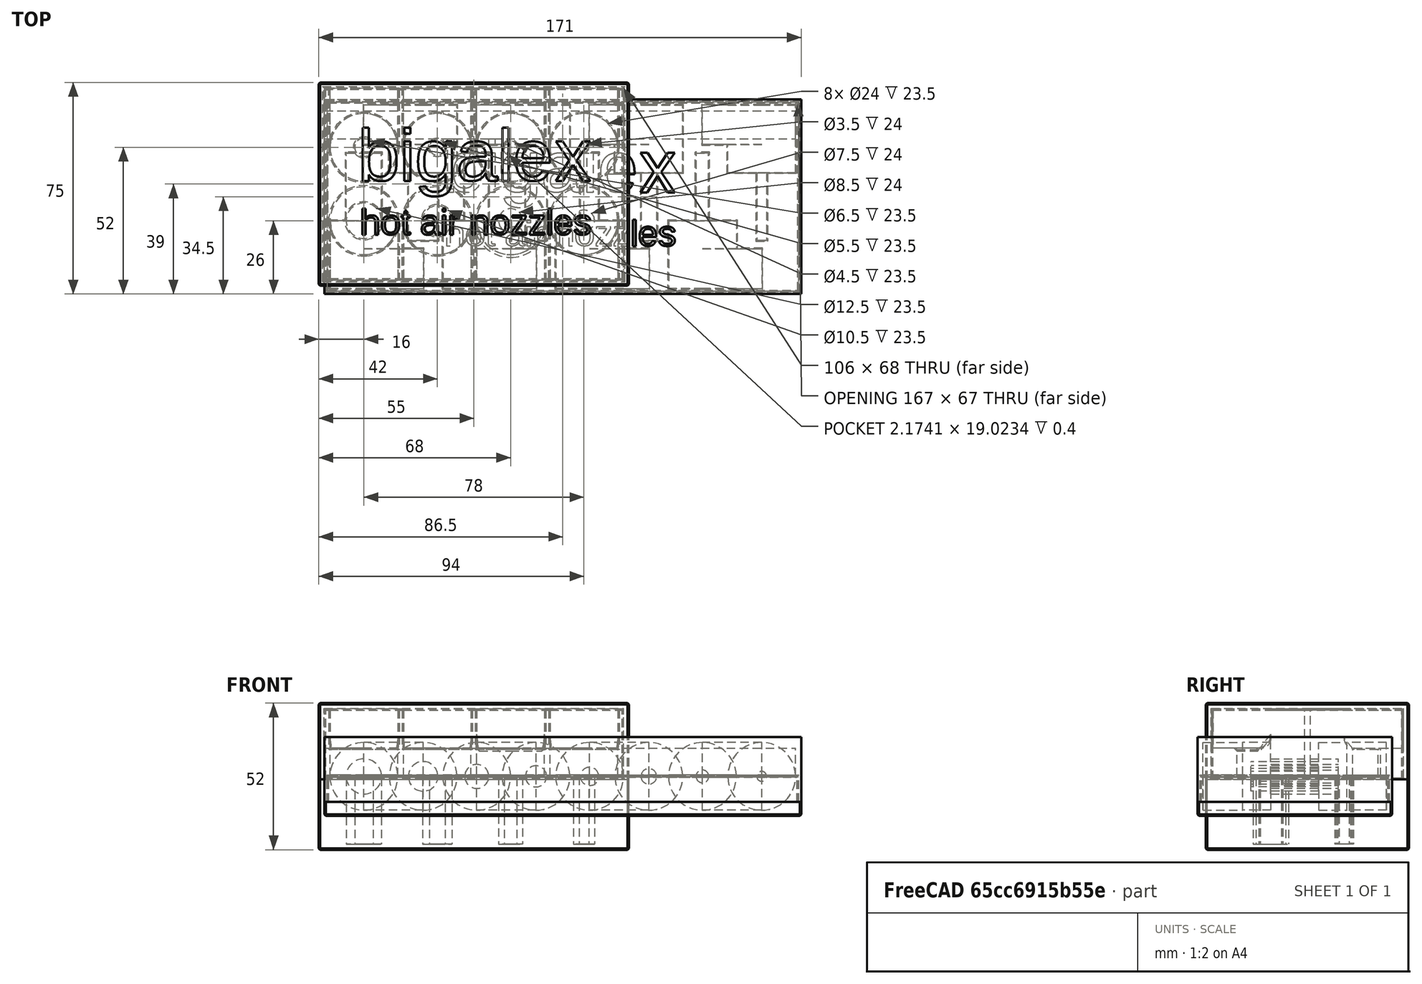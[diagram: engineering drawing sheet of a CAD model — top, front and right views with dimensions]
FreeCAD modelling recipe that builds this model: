
FCSTD DOCUMENT  (FreeCAD 0.18R16093 (Git))
Label: hotair
License: All rights reserved
LicenseURL: http://en.wikipedia.org/wiki/All_rights_reserved
objects: Part::Cylinder×32, Part::Box×27, Part::MultiFuse×26, Part::Cut×8, Part::Part2DObjectPython×6, Part::Extrusion×6, Part::Chamfer×5, Part::FeaturePython×3, PartDesign::Body×1
note: 114 computed .brp shape members not serialized (recipe doc carries the construction recipe); baked Part::Feature solids carry a one-line shape summary decoded from their .brp

FEATURE [PartDesign::Body] Body
  Origin = -> Origin
FEATURE [Part::Cylinder] Cylinder  label="smallcyl"
  Angle = 360
  AttacherType = Attacher::AttachEngine3D
  Height = 24
  Placement = pos=(0,0,0) rot=(1,0,0;1.5708rad)
  Radius = 12
FEATURE [Part::Cylinder] Cylinder001  label="bigcyl"
  Angle = 360
  AttacherType = Attacher::AttachEngine3D
  Height = 24
  Placement = pos=(0,0,0) rot=(-1,0,0;1.5708rad)
  Radius = 5.25
FEATURE [Part::Box] Box  label="Cube"
  AttacherType = Attacher::AttachEngine3D
  Height = 24
  Length = 21
  Placement = pos=(0,-24,-12) rot=(0,0,1;0rad)
  Width = 14
FEATURE [Part::MultiFuse] Fusion
  Placement = pos=(21,17,0) rot=(0,0,1;3.14159rad)
  Shapes = -> [Cylinder,Cylinder001,Box]
FEATURE [Part::Box] Box001  label="Cube001"
  AttacherType = Attacher::AttachEngine3D
  Height = 24
  Length = 21
  Placement = pos=(0,-24,-12) rot=(0,0,1;0rad)
  Width = 14
FEATURE [Part::Cylinder] Cylinder002  label="smallcyl001"
  Angle = 360
  AttacherType = Attacher::AttachEngine3D
  Height = 24
  Placement = pos=(0,0,0) rot=(1,0,0;1.5708rad)
  Radius = 12
FEATURE [Part::Cylinder] Cylinder003  label="bigcyl001"
  Angle = 360
  AttacherType = Attacher::AttachEngine3D
  Height = 24
  Placement = pos=(0,0,0) rot=(-1,0,0;1.5708rad)
  Radius = 6.25
FEATURE [Part::MultiFuse] Fusion001
  Shapes = -> [Cylinder002,Cylinder003,Box001]
FEATURE [Part::MultiFuse] Fusion002
  Shapes = -> [Fusion,Fusion001]
FEATURE [Part::Cylinder] Cylinder004  label="smallcyl002"
  Angle = 360
  AttacherType = Attacher::AttachEngine3D
  Height = 24
  Placement = pos=(0,0,0) rot=(1,0,0;1.5708rad)
  Radius = 12
FEATURE [Part::Box] Box002  label="Cube002"
  AttacherType = Attacher::AttachEngine3D
  Height = 24
  Length = 21
  Placement = pos=(0,-24,-12) rot=(0,0,1;0rad)
  Width = 14
FEATURE [Part::Box] Box003  label="Cube003"
  AttacherType = Attacher::AttachEngine3D
  Height = 24
  Length = 21
  Placement = pos=(0,-24,-12) rot=(0,0,1;0rad)
  Width = 14
FEATURE [Part::Cylinder] Cylinder005  label="smallcyl003"
  Angle = 360
  AttacherType = Attacher::AttachEngine3D
  Height = 24
  Placement = pos=(0,0,0) rot=(1,0,0;1.5708rad)
  Radius = 12
FEATURE [Part::Cylinder] Cylinder006  label="bigcyl002"
  Angle = 360
  AttacherType = Attacher::AttachEngine3D
  Height = 24
  Placement = pos=(0,0,0) rot=(-1,0,0;1.5708rad)
  Radius = 3.75
FEATURE [Part::MultiFuse] Fusion003
  Placement = pos=(21,17,0) rot=(0,0,1;3.14159rad)
  Shapes = -> [Cylinder005,Cylinder006,Box003]
FEATURE [Part::Cylinder] Cylinder007  label="bigcyl003"
  Angle = 360
  AttacherType = Attacher::AttachEngine3D
  Height = 24
  Placement = pos=(0,0,0) rot=(-1,0,0;1.5708rad)
  Radius = 4.25
FEATURE [Part::MultiFuse] Fusion004
  Shapes = -> [Cylinder004,Cylinder007,Box002]
FEATURE [Part::MultiFuse] Fusion005
  Placement = pos=(40,0,0) rot=(0,0,1;0rad)
  Shapes = -> [Fusion003,Fusion004]
FEATURE [Part::Cylinder] Cylinder008  label="smallcyl004"
  Angle = 360
  AttacherType = Attacher::AttachEngine3D
  Height = 24
  Placement = pos=(0,0,0) rot=(1,0,0;1.5708rad)
  Radius = 12
FEATURE [Part::Box] Box004  label="Cube004"
  AttacherType = Attacher::AttachEngine3D
  Height = 24
  Length = 21
  Placement = pos=(0,-24,-12) rot=(0,0,1;0rad)
  Width = 14
FEATURE [Part::Box] Box005  label="Cube005"
  AttacherType = Attacher::AttachEngine3D
  Height = 24
  Length = 21
  Placement = pos=(0,-24,-12) rot=(0,0,1;0rad)
  Width = 14
FEATURE [Part::Cylinder] Cylinder009  label="smallcyl005"
  Angle = 360
  AttacherType = Attacher::AttachEngine3D
  Height = 24
  Placement = pos=(0,0,0) rot=(1,0,0;1.5708rad)
  Radius = 12
FEATURE [Part::Cylinder] Cylinder010  label="bigcyl004"
  Angle = 360
  AttacherType = Attacher::AttachEngine3D
  Height = 24
  Placement = pos=(0,0,0) rot=(-1,0,0;1.5708rad)
  Radius = 2.75
FEATURE [Part::MultiFuse] Fusion006
  Placement = pos=(21,17,0) rot=(0,0,1;3.14159rad)
  Shapes = -> [Cylinder009,Cylinder010,Box005]
FEATURE [Part::Cylinder] Cylinder011  label="bigcyl005"
  Angle = 360
  AttacherType = Attacher::AttachEngine3D
  Height = 24
  Placement = pos=(0,0,0) rot=(-1,0,0;1.5708rad)
  Radius = 3.25
FEATURE [Part::MultiFuse] Fusion007
  Shapes = -> [Cylinder008,Cylinder011,Box004]
FEATURE [Part::MultiFuse] Fusion008
  Placement = pos=(80,0,0) rot=(0,0,1;0rad)
  Shapes = -> [Fusion006,Fusion007]
FEATURE [Part::Cylinder] Cylinder012  label="smallcyl006"
  Angle = 360
  AttacherType = Attacher::AttachEngine3D
  Height = 24
  Placement = pos=(0,0,0) rot=(1,0,0;1.5708rad)
  Radius = 12
FEATURE [Part::Box] Box006  label="Cube006"
  AttacherType = Attacher::AttachEngine3D
  Height = 24
  Length = 21
  Placement = pos=(0,-24,-12) rot=(0,0,1;0rad)
  Width = 14
FEATURE [Part::Box] Box007  label="Cube007"
  AttacherType = Attacher::AttachEngine3D
  Height = 24
  Length = 21
  Placement = pos=(0,-24,-12) rot=(0,0,1;0rad)
  Width = 14
FEATURE [Part::Cylinder] Cylinder013  label="smallcyl007"
  Angle = 360
  AttacherType = Attacher::AttachEngine3D
  Height = 24
  Placement = pos=(0,0,0) rot=(1,0,0;1.5708rad)
  Radius = 12
FEATURE [Part::Cylinder] Cylinder014  label="bigcyl006"
  Angle = 360
  AttacherType = Attacher::AttachEngine3D
  Height = 24
  Placement = pos=(0,0,0) rot=(-1,0,0;1.5708rad)
  Radius = 1.75
FEATURE [Part::MultiFuse] Fusion009
  Placement = pos=(21,17,0) rot=(0,0,1;3.14159rad)
  Shapes = -> [Cylinder013,Cylinder014,Box007]
FEATURE [Part::Cylinder] Cylinder015  label="bigcyl007"
  Angle = 360
  AttacherType = Attacher::AttachEngine3D
  Height = 24
  Placement = pos=(0,0,0) rot=(-1,0,0;1.5708rad)
  Radius = 2.25
FEATURE [Part::MultiFuse] Fusion010
  Shapes = -> [Cylinder012,Cylinder015,Box006]
FEATURE [Part::MultiFuse] Fusion011
  Placement = pos=(120,0,0) rot=(0,0,1;0rad)
  Shapes = -> [Fusion009,Fusion010]
FEATURE [Part::Box] Box008  label="Cube008"
  AttacherType = Attacher::AttachEngine3D
  Height = 10
  Length = 167
  Placement = pos=(-14,29,0) rot=(0,0,1;0rad)
  Width = 10
FEATURE [Part::Cylinder] Cylinder016  label="smallcyl008"
  Angle = 360
  AttacherType = Attacher::AttachEngine3D
  Height = 24
  Placement = pos=(0,0,0) rot=(1,0,0;1.5708rad)
  Radius = 12
FEATURE [Part::Box] Box009  label="Cube009"
  AttacherType = Attacher::AttachEngine3D
  Height = 24
  Length = 21
  Placement = pos=(0,-24,-12) rot=(0,0,1;0rad)
  Width = 14
FEATURE [Part::Cylinder] Cylinder017  label="bigcyl008"
  Angle = 360
  AttacherType = Attacher::AttachEngine3D
  Height = 24
  Placement = pos=(0,0,0) rot=(-1,0,0;1.5708rad)
  Radius = 6.25
FEATURE [Part::MultiFuse] Fusion013  label="nozzle000"
  Placement = pos=(0,0,0) rot=(0.57735,-0.57735,0.57735;4.18879rad)
  Shapes = -> [Cylinder016,Cylinder017,Box009]
FEATURE [Part::Cylinder] Cylinder018  label="bigcyl009"
  Angle = 360
  AttacherType = Attacher::AttachEngine3D
  Height = 24
  Placement = pos=(0,0,0) rot=(-1,0,0;1.5708rad)
  Radius = 3.25
FEATURE [Part::Box] Box010  label="Cube010"
  AttacherType = Attacher::AttachEngine3D
  Height = 24
  Length = 21
  Placement = pos=(0,-24,-12) rot=(0,0,1;0rad)
  Width = 14
FEATURE [Part::Cylinder] Cylinder019  label="smallcyl009"
  Angle = 360
  AttacherType = Attacher::AttachEngine3D
  Height = 24
  Placement = pos=(0,0,0) rot=(1,0,0;1.5708rad)
  Radius = 12
FEATURE [Part::MultiFuse] Fusion014  label="nozzle001"
  Placement = pos=(0,26,0) rot=(0.57735,0.57735,-0.57735;4.18879rad)
  Shapes = -> [Cylinder019,Cylinder018,Box010]
FEATURE [Part::Cylinder] Cylinder020  label="bigcyl010"
  Angle = 360
  AttacherType = Attacher::AttachEngine3D
  Height = 24
  Placement = pos=(0,0,0) rot=(-1,0,0;1.5708rad)
  Radius = 5.25
FEATURE [Part::Box] Box011  label="Cube011"
  AttacherType = Attacher::AttachEngine3D
  Height = 24
  Length = 21
  Placement = pos=(0,-24,-12) rot=(0,0,1;0rad)
  Width = 14
FEATURE [Part::Cylinder] Cylinder021  label="smallcyl010"
  Angle = 360
  AttacherType = Attacher::AttachEngine3D
  Height = 24
  Placement = pos=(0,0,0) rot=(1,0,0;1.5708rad)
  Radius = 12
FEATURE [Part::Cylinder] Cylinder022  label="bigcyl011"
  Angle = 360
  AttacherType = Attacher::AttachEngine3D
  Height = 24
  Placement = pos=(0,0,0) rot=(-1,0,0;1.5708rad)
  Radius = 2.75
FEATURE [Part::Cylinder] Cylinder023  label="smallcyl011"
  Angle = 360
  AttacherType = Attacher::AttachEngine3D
  Height = 24
  Placement = pos=(0,0,0) rot=(1,0,0;1.5708rad)
  Radius = 12
FEATURE [Part::MultiFuse] Fusion015  label="nozzle002"
  Placement = pos=(26,0,0) rot=(0.57735,-0.57735,0.57735;4.18879rad)
  Shapes = -> [Cylinder023,Cylinder020,Box011]
FEATURE [Part::Box] Box012  label="Cube012"
  AttacherType = Attacher::AttachEngine3D
  Height = 24
  Length = 21
  Placement = pos=(0,-24,-12) rot=(0,0,1;0rad)
  Width = 14
FEATURE [Part::MultiFuse] Fusion016  label="nozzle003"
  Placement = pos=(26,26,0) rot=(0.57735,0.57735,-0.57735;4.18879rad)
  Shapes = -> [Cylinder021,Cylinder022,Box012]
FEATURE [Part::Cylinder] Cylinder024  label="bigcyl012"
  Angle = 360
  AttacherType = Attacher::AttachEngine3D
  Height = 24
  Placement = pos=(0,0,0) rot=(-1,0,0;1.5708rad)
  Radius = 4.25
FEATURE [Part::Box] Box013  label="Cube013"
  AttacherType = Attacher::AttachEngine3D
  Height = 24
  Length = 21
  Placement = pos=(0,-24,-12) rot=(0,0,1;0rad)
  Width = 14
FEATURE [Part::Cylinder] Cylinder025  label="smallcyl012"
  Angle = 360
  AttacherType = Attacher::AttachEngine3D
  Height = 24
  Placement = pos=(0,0,0) rot=(1,0,0;1.5708rad)
  Radius = 12
FEATURE [Part::Cylinder] Cylinder026  label="bigcyl013"
  Angle = 360
  AttacherType = Attacher::AttachEngine3D
  Height = 24
  Placement = pos=(0,0,0) rot=(-1,0,0;1.5708rad)
  Radius = 2.25
FEATURE [Part::Cylinder] Cylinder027  label="smallcyl013"
  Angle = 360
  AttacherType = Attacher::AttachEngine3D
  Height = 24
  Placement = pos=(0,0,0) rot=(1,0,0;1.5708rad)
  Radius = 12
FEATURE [Part::MultiFuse] Fusion017  label="nozzle004"
  Placement = pos=(52,0,0) rot=(0.57735,-0.57735,0.57735;4.18879rad)
  Shapes = -> [Cylinder027,Cylinder024,Box013]
FEATURE [Part::Box] Box014  label="Cube014"
  AttacherType = Attacher::AttachEngine3D
  Height = 24
  Length = 21
  Placement = pos=(0,-24,-12) rot=(0,0,1;0rad)
  Width = 14
FEATURE [Part::MultiFuse] Fusion018  label="nozzle005"
  Placement = pos=(52,26,0) rot=(0.57735,0.57735,-0.57735;4.18879rad)
  Shapes = -> [Cylinder025,Cylinder026,Box014]
FEATURE [Part::Cylinder] Cylinder028  label="bigcyl014"
  Angle = 360
  AttacherType = Attacher::AttachEngine3D
  Height = 24
  Placement = pos=(0,0,0) rot=(-1,0,0;1.5708rad)
  Radius = 3.75
FEATURE [Part::Box] Box015  label="Cube015"
  AttacherType = Attacher::AttachEngine3D
  Height = 24
  Length = 21
  Placement = pos=(0,-24,-12) rot=(0,0,1;0rad)
  Width = 14
FEATURE [Part::Cylinder] Cylinder029  label="smallcyl014"
  Angle = 360
  AttacherType = Attacher::AttachEngine3D
  Height = 24
  Placement = pos=(0,0,0) rot=(1,0,0;1.5708rad)
  Radius = 12
FEATURE [Part::Cylinder] Cylinder030  label="bigcyl015"
  Angle = 360
  AttacherType = Attacher::AttachEngine3D
  Height = 24
  Placement = pos=(0,0,0) rot=(-1,0,0;1.5708rad)
  Radius = 1.75
FEATURE [Part::Cylinder] Cylinder031  label="smallcyl015"
  Angle = 360
  AttacherType = Attacher::AttachEngine3D
  Height = 24
  Placement = pos=(0,0,0) rot=(1,0,0;1.5708rad)
  Radius = 12
FEATURE [Part::MultiFuse] Fusion019  label="nozzle006"
  Placement = pos=(78,0,0) rot=(0.57735,-0.57735,0.57735;4.18879rad)
  Shapes = -> [Cylinder031,Cylinder028,Box015]
FEATURE [Part::Box] Box016  label="Cube016"
  AttacherType = Attacher::AttachEngine3D
  Height = 24
  Length = 21
  Placement = pos=(0,-24,-12) rot=(0,0,1;0rad)
  Width = 14
FEATURE [Part::MultiFuse] Fusion020  label="nozzle007"
  Placement = pos=(78,26,0) rot=(0.57735,0.57735,-0.57735;4.18879rad)
  Shapes = -> [Cylinder029,Cylinder030,Box016]
FEATURE [Part::MultiFuse] Fusion021  label="nozzles2"
  Shapes = -> [Fusion013,Fusion014,Fusion015,Fusion016,Fusion017,Fusion018,Fusion019,Fusion020]
FEATURE [Part::Box] Box017  label="Cube017"
  AttacherType = Attacher::AttachEngine3D
  Height = 50
  Length = 106
  Placement = pos=(-14,-21,-26) rot=(0,0,1;0rad)
  Width = 68
FEATURE [Part::Box] Box018  label="lidkeepout"
  AttacherType = Attacher::AttachEngine3D
  Height = 25.1
  Length = 106.2
  Placement = pos=(-14.1,-21.1,-1) rot=(0,0,1;0rad)
  Width = 68.2
FEATURE [Part::Box] Box019  label="Cube018"
  AttacherType = Attacher::AttachEngine3D
  Height = 27
  Length = 110
  Placement = pos=(-16,-23,-1) rot=(0,0,1;0rad)
  Width = 72
FEATURE [Part::Box] Box020  label="Cube019"
  AttacherType = Attacher::AttachEngine3D
  Height = 25
  Length = 110
  Placement = pos=(-16,-23,-26) rot=(0,0,1;0rad)
  Width = 72
FEATURE [Part::Cut] Cut
  Base = -> Box019
  Tool = -> Box018
FEATURE [Part::MultiFuse] Fusion022
  Shapes = -> [Box017,Box020]
FEATURE [Part::Cut] Cut001
  Base = -> Fusion022
  Tool = -> Fusion021
FEATURE [Part::Part2DObjectPython] ShapeString  # Draft 2D object (typed FeaturePython)
  FontFile = <path>
  Placement = pos=(-2,14,26) rot=(0,0,1;0rad)
  Size = 20
  String = bigalex
  Tracking = 0
FEATURE [Part::Part2DObjectPython] ShapeString001  # Draft 2D object (typed FeaturePython)
  FontFile = <path>
  Placement = pos=(-1.3,-5,26) rot=(0,0,1;0rad)
  Size = 9.77
  String = hot air nozzles
  Tracking = 0
FEATURE [Part::Extrusion] Extrude
  Base = -> ShapeString
  Dir = (0,0,1)
  DirMode = 2
  FaceMakerClass = Part::FaceMakerBullseye
  LengthFwd = 0
  LengthRev = 0.4
  Solid = false
  Symmetric = false
FEATURE [Part::Extrusion] Extrude001
  Base = -> ShapeString001
  Dir = (0,0,1)
  DirMode = 2
  FaceMakerClass = Part::FaceMakerBullseye
  LengthFwd = 0
  LengthRev = 0.4
  Solid = false
  Symmetric = false
FEATURE [Part::FeaturePython] BooleanFragments  # WARN: FeaturePython — macro-defined, semantics opaque (R4)
  Mode = 0
  Objects = -> [Extrude,Extrude001]
  Tolerance = 0
FEATURE [Part::Cut] Cut002
  Base = -> Cut
  Tool = -> BooleanFragments
FEATURE [Part::Chamfer] Chamfer  label="box1_top"
  Base = -> Cut002
  Edges = 12 edges r=0.5: [Edge1,Edge2,Edge3,Edge6,Edge7,Edge8,Edge9,Edge429,Edge431,Edge432,Edge433,Edge434]
FEATURE [Part::Chamfer] Chamfer001  label="box1_bottom"
  Base = -> Cut001
  Edges = 92 edges: [Edge5 r=0.5,Edge6 r=0.5,Edge7 r=0.5,Edge8 r=0.5,Edge9 r=0.5,Edge11 r=0.5,Edge12 r=0.5,Edge14 r=0.5,Edge21 r=0.5,Edge22 r=0.5,Edge23 r=0.5,Edge24 r=0.5,Edge25 r=0.5,Edge26 r=0.5,Edge27 r=0.5,Edge28 r=0.5,Edge29 r=0.5,Edge30 r=0.5,Edge31 r=0.5,Edge32 r=0.5,Edge33 r=0.5,Edge34 r=0.5,Edge35 r=0.5,Edge36 r=0.5,Edge37 r=0.5,Edge38 r=0.5,Edge39 r=0.5,Edge40 r=0.5,Edge41 r=0.5,Edge42 r=0.5,Edge43 r=0.5,Edge44 r=0.5,Edge45 r=0.5,Edge46 r=0.5,Edge47 r=0.5,Edge48 r=0.5,Edge49 r=0.5,Edge50 r=0.5,Edge51 r=0.5,Edge52 r=0.5,Edge53 r=0.5,Edge54 r=0.5,Edge55 r=0.5,Edge56 r=0.5,Edge57 r=0.5,Edge58 r=0.5,+46 more]
FEATURE [Part::Box] Box023  label="Cube022"
  AttacherType = Attacher::AttachEngine3D
  Height = 14
  Length = 167
  Placement = pos=(-13,-25,-14) rot=(0,0,1;0rad)
  Width = 67
FEATURE [Part::Box] Box024  label="lidkeepout001"
  AttacherType = Attacher::AttachEngine3D
  Height = 25.1
  Length = 106.2
  Placement = pos=(-14.1,-21.1,-1) rot=(0,0,1;0rad)
  Width = 68.2
FEATURE [Part::Box] Box032  label="Cube030"
  AttacherType = Attacher::AttachEngine3D
  Height = 27
  Length = 110
  Placement = pos=(-16,-23,-1) rot=(0,0,1;0rad)
  Width = 72
FEATURE [Part::Cut] Cut003
  Base = -> Box032
  Tool = -> Box024
FEATURE [Part::Part2DObjectPython] ShapeString002  # Draft 2D object (typed FeaturePython)
  FontFile = <path>
  Placement = pos=(-1.3,-5,26) rot=(0,0,1;0rad)
  Size = 9.77
  String = hot air nozzles
  Tracking = 0
FEATURE [Part::Part2DObjectPython] ShapeString003  # Draft 2D object (typed FeaturePython)
  FontFile = <path>
  Placement = pos=(-2,14,26) rot=(0,0,1;0rad)
  Size = 20
  String = bigalex
  Tracking = 0
FEATURE [Part::Extrusion] Extrude002
  Base = -> ShapeString003
  Dir = (0,0,1)
  DirMode = 2
  FaceMakerClass = Part::FaceMakerBullseye
  LengthFwd = 0
  LengthRev = 0.2
  Solid = false
  Symmetric = false
FEATURE [Part::Extrusion] Extrude003
  Base = -> ShapeString002
  Dir = (0,0,1)
  DirMode = 2
  FaceMakerClass = Part::FaceMakerBullseye
  LengthFwd = 0
  LengthRev = 0.2
  Solid = false
  Symmetric = false
FEATURE [Part::FeaturePython] BooleanFragments001  # WARN: FeaturePython — macro-defined, semantics opaque (R4)
  Mode = 0
  Objects = -> [Extrude002,Extrude003]
  Tolerance = 0
FEATURE [Part::Cut] Cut005
  Base = -> Cut003
  Tool = -> BooleanFragments001
FEATURE [Part::Chamfer] Chamfer003  label="box2_top"
  Base = -> Cut005
  Edges = 12 edges r=0.5: [Edge1,Edge2,Edge3,Edge6,Edge7,Edge8,Edge9,Edge429,Edge431,Edge432,Edge433,Edge434]
FEATURE [Part::Box] Box034  label="Cube032"
  AttacherType = Attacher::AttachEngine3D
  Height = 5
  Length = 169
  Placement = pos=(-14,-26,-14) rot=(0,0,1;0rad)
  Width = 69
FEATURE [Part::MultiFuse] Fusion029
  Shapes = -> [Box023,Box034]
FEATURE [Part::Box] Box035  label="Cube033"
  AttacherType = Attacher::AttachEngine3D
  Height = 23
  Length = 169
  Placement = pos=(-14,-26,-9) rot=(0,0,1;0rad)
  Width = 69
FEATURE [Part::Box] Box036  label="keepout"
  AttacherType = Attacher::AttachEngine3D
  Height = 14.5
  Length = 167.2
  Placement = pos=(-13.1,-25.1,-14) rot=(0,0,1;0rad)
  Width = 67.2
FEATURE [Part::MultiFuse] Fusion012  label="nozzles001"
  Shapes = -> [Fusion002,Fusion005,Fusion008,Fusion011]
FEATURE [Part::MultiFuse] Fusion027  label="nozzles002"
  Shapes = -> [Fusion012]
FEATURE [Part::Cut] Cut004  label="box2_bottom"
  Base = -> Fusion029
  Tool = -> Fusion027
FEATURE [Part::MultiFuse] Fusion030
  Shapes = -> [Fusion027,Box036]
FEATURE [Part::Cut] Cut007  label="top2"
  Base = -> Box035
  Tool = -> Fusion030
FEATURE [Part::Part2DObjectPython] ShapeString004  # Draft 2D object (typed FeaturePython)
  FontFile = <path>
  Placement = pos=(-2,14,14) rot=(0,0,1;0rad)
  Size = 20
  String = bigalex
  Tracking = 0
FEATURE [Part::Extrusion] Extrude004
  Base = -> ShapeString004
  Dir = (0,0,1)
  DirMode = 2
  FaceMakerClass = Part::FaceMakerBullseye
  LengthFwd = 0
  LengthRev = 0.2
  Solid = false
  Symmetric = false
FEATURE [Part::Part2DObjectPython] ShapeString005  # Draft 2D object (typed FeaturePython)
  FontFile = <path>
  Placement = pos=(-1.3,-5,14) rot=(0,0,1;0rad)
  Size = 9.77
  String = hot air nozzles
  Tracking = 0
FEATURE [Part::Extrusion] Extrude005
  Base = -> ShapeString005
  Dir = (0,0,1)
  DirMode = 2
  FaceMakerClass = Part::FaceMakerBullseye
  LengthFwd = 0
  LengthRev = 0.2
  Solid = false
  Symmetric = false
FEATURE [Part::FeaturePython] BooleanFragments002  # WARN: FeaturePython — macro-defined, semantics opaque (R4)
  Mode = 0
  Objects = -> [Extrude004,Extrude005]
  Placement = pos=(30,-4,0) rot=(0,0,1;0rad)
  Tolerance = 0
FEATURE [Part::Cut] Cut008
  Base = -> Cut007
  Tool = -> BooleanFragments002
FEATURE [Part::Chamfer] Chamfer004
  Base = -> Cut004
  Edges = 7 edges r=1: [Edge5,Edge6,Edge7,Edge8,Edge9,Edge11,Edge14]
FEATURE [Part::Chamfer] Chamfer005
  Base = -> Chamfer004
  Edges = 12 edges r=1: [Edge1,Edge4,Edge5,Edge17,Edge121,Edge122,Edge123,Edge124,Edge125,Edge126,Edge127,Edge128]
note: 6 file-system paths scrubbed to <path> (originals preserved in the JSON sidecar)
